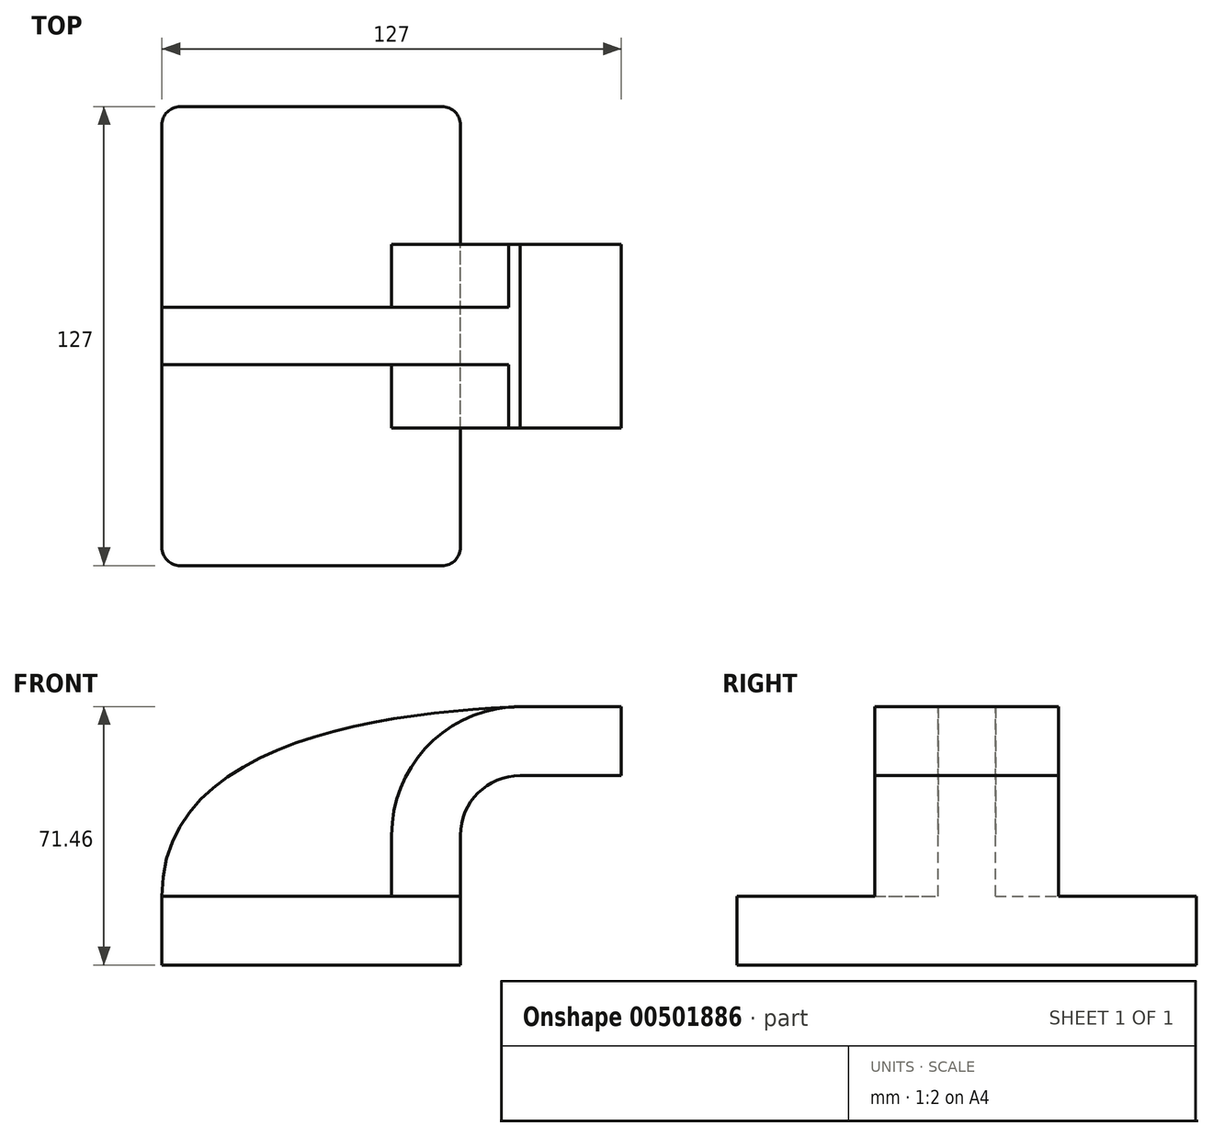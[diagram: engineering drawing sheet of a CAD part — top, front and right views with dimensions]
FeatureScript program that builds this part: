
annotation { "Feature Type Name" : "Feature", "Feature Type Description" : "" }
export const myFeature = defineFeature(function(context is Context, id is Id, definition is map)
    precondition{}
    {
        {
            var Q0;
            Q0=qCreatedBy(makeId("Front.planeOp"),FACE);
            var sketch = newSketch(context, id + "F0", { "sketchPlane" : qUnion([Q0])});
            skLineSegment(sketch, "E0.bottom", {"start": v(-41.28, 9.52) * mm, "end": v(41.28, 9.53) * mm});
            skLineSegment(sketch, "E0.top", {"start": v(-41.28, -9.53) * mm, "end": v(41.28, -9.53) * mm});
            skLineSegment(sketch, "E0.left", {"start": v(-41.28, 9.52) * mm, "end": v(-41.28, -9.53) * mm});
            skLineSegment(sketch, "E0.right", {"start": v(41.28, 9.53) * mm, "end": v(41.28, -9.52) * mm});
            skPoint(sketch, "E0.middle", {"position": v(0, 0) * mm});
            skLineSegment(sketch, "E1.bottom", {"start": v(112.01, 38.1) * mm, "end": v(61.21, 38.1) * mm});
            skLineSegment(sketch, "E1.top", {"start": v(112.01, 66.67) * mm, "end": v(61.21, 66.67) * mm});
            skLineSegment(sketch, "E1.left", {"start": v(112.01, 38.1) * mm, "end": v(112.01, 66.67) * mm});
            skLineSegment(sketch, "E1.right", {"start": v(61.21, 38.1) * mm, "end": v(61.21, 66.67) * mm});
            skPoint(sketch, "E1.middle", {"position": v(86.61, 52.39) * mm});
            skLineSegment(sketch, "E2", {"start": v(41.27, 9.53) * mm, "end": v(41.27, 26.37) * mm});
            skArc(sketch, "E3", {"start": v(41.27, 26.37) * mm, "mid": v(46.11, 38.04) * mm, "end": v(57.78, 42.88) * mm});
            skLineSegment(sketch, "E4", {"start": v(57.78, 42.88) * mm, "end": v(85.73, 42.88) * mm});
            skLineSegment(sketch, "E5.0", {"start": v(57.78, 61.93) * mm, "end": v(85.73, 61.93) * mm});
            skArc(sketch, "E5.1", {"start": v(22.22, 26.37) * mm, "mid": v(32.64, 51.5) * mm, "end": v(57.78, 61.93) * mm});
            skLineSegment(sketch, "E5.2", {"start": v(22.22, 9.53) * mm, "end": v(22.22, 26.37) * mm});
            skLineSegment(sketch, "E6", {"start": v(85.73, 42.88) * mm, "end": v(85.73, 61.93) * mm});
            skFitSpline(sketch, "E7", {"points": [v(-41.28, 9.52) * mm, v(57.78, 61.93) * mm], "startDerivative": vector(0.01, 131.14) * mm, "endDerivative": vector(107.5, 4.48) * mm});
            skSolve(sketch);
        }
        {
            var Q0;
            Q0=makeQuery(id+"F0.imprint","IMPRINT",FACE,{"disambiguationData":[TD([[makeQuery(id+"F0.imprint","IMPRINT",EDGE,{"derivedFrom":sQuery(id+"F0.wireOp",EDGE,"E0.top")}),1.0]])]});
            extrude(context, id + "F1", {"entities" : qUnion([Q0]), "endBound" : BoundingType.SYMMETRIC, "depth" : 127 * mm});
        }
        {
            var Q0;
            {var subQ1=sQuery(id+"F0.wireOp",EDGE,"E2");Q0=makeQuery(id+"F0.imprint","IMPRINT",FACE,{"disambiguationData":[TD([[makeQuery(id+"F0.imprint","IMPRINT",EDGE,{"derivedFrom":subQ1}),1.0]])]});}
            var Q1;
            {var subQ5=sQuery(id+"F0.wireOp",EDGE,"E6");Q1=makeQuery(id+"F0.imprint","IMPRINT",FACE,{"disambiguationData":[TD([[makeQuery(id+"F0.imprint","IMPRINT",EDGE,{"derivedFrom":subQ5}),1.0]])]});}
            extrude(context, id + "F2", {"entities" : qUnion([Q0, Q1]), "operationType" : NewBodyOperationType.ADD, "endBound" : BoundingType.SYMMETRIC, "depth" : 50.8 * mm});
        }
        {
            var Q0;
            {var subQ3=sQuery(id+"F0.wireOp",EDGE,"E5.2");Q0=makeQuery(id+"F0.imprint","IMPRINT",FACE,{"disambiguationData":[TD([[makeQuery(id+"F0.imprint","IMPRINT",EDGE,{"derivedFrom":subQ3}),1.0]])]});}
            extrude(context, id + "F3", {"entities" : qUnion([Q0]), "operationType" : NewBodyOperationType.ADD, "endBound" : BoundingType.SYMMETRIC, "depth" : 15.88 * mm});
        }
        {
            var Q0;
            Q0=makeQuery(id+"F1.opExtrude","CAP_EDGE",EDGE,{"disambiguationData":[OSD([sQuery(id+"F0.wireOp",EDGE,"E0.right")])],"isStart":false});
            var Q1;
            Q1=makeQuery(id+"F1.opExtrude","CAP_EDGE",EDGE,{"disambiguationData":[OSD([sQuery(id+"F0.wireOp",EDGE,"E0.right")])],"isStart":true});
            var Q2;
            Q2=makeQuery(id+"F1.opExtrude","CAP_EDGE",EDGE,{"disambiguationData":[OSD([sQuery(id+"F0.wireOp",EDGE,"E0.left")])],"isStart":false});
            var Q3;
            Q3=makeQuery(id+"F1.opExtrude","CAP_EDGE",EDGE,{"disambiguationData":[OSD([sQuery(id+"F0.wireOp",EDGE,"E0.left")])],"isStart":true});
            fillet(context, id + "F4", {"entities" : qUnion([Q0, Q1, Q2, Q3]), "radius" : 5.08 * mm, "tangentPropagation" : true, "allowEdgeOverflow" : false});
        }
    });
